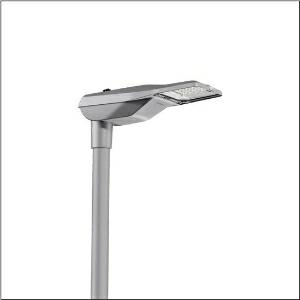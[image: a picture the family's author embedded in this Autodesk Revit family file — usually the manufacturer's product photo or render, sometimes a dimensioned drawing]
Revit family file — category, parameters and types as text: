
# Revit family: streetlight_sl_21_iq_micro___st1_0a_5xe1d31v08db_4967
name_source: partatom
category: Lighting Fixtures
units: mm (PartAtom-declared; Revit-internal decimal feet)

## family parameters
Cut with Voids When Loaded = No
Host = Face
Light Source = No
Part Type = Normal
Room Calculation Point = No
Round Connector Dimension = Use Diameter
Shared = No

## types (1)
- --- (1 x LED, 5110 lm, 39.1 W, 3000K)
    Apparent Load = 39 VA
    CIE Flux Codes = 37 72 97 100 100
    Color Rendering = 70
    Color Temperature = 3000K
    Default Elevation = 1800 mm
    Description = Streetlight SL 21 iQ micro, mast luminaire, primary light control with lens, of PMMA, primary optical cover: cover, of toughened safety glass, transparent, light distribution: ST1.0a, light emission: direct distribution, primary light characteristic: asymmetric, installation type: post-top, side-entry, LED, High Power LED, rated luminous flux: 5.110lm, luminous efficacy: 131lm/W, light colour: 730, colour temperature: 3000K, control gear: iQ-Street Remote, D4i with power reduction, control: pre-setting: logarithmic dimming characteristic, Street-Remote, Auto-Match, Temp-Guard, Lumen-Switch, Night-Set, Smart-Wire, Light-Fading, Desk-Remote (wireless, voltage-free reading and setting of iQ features in the workshop via application-optimized NFC function/RFID function), optimised constant luminous flux control (CLO 2.0), mains connection: 220..240V, AC, 50/60Hz, start of lifetime: 39W, end of service life: 41W, reduction: 17W, luminaire housing, of diecast aluminium, powder-coated, SITECO metallic grey (DB 702S), corrosivity category C5 high according to DIN EN ISO 12944, please order mast flange separately, inclination adjustable: 0°, 5°, 10°, 15°, sealing non-destructively replaceable, multi-level sealing system, length: 528mm, width: 235mm, height: 110mm, mast flange for spigot size: 42mm (side-entry): 5XC10008XM4, 60/48mm (side-entry/post-top): 5XC10108XM2, 76/60mm (side-entry/post-top): 5XC10108XM1, mounting height: 4..8m, Smart Interface above, protection rating (complete): IP66, insulation class (complete): insulation class II (safety insulation), certification: CE, ENEC, ENEC+, VDE, impact resistance: IK10, permissible operating ambient temperature for outdoor applications: -40..+50°C, standard-compliant lighting for roads and squares, packaging unit: 1 piece

Light Distribution: ST1.0a
    Height = 110 mm
    Lamp = 1 x LED
    Lamp Light Flux = 5110 lm
    Lamp Power = 39.1 W
    Lamp count = 1
    Length = 528 mm
    Luminous efficacy = 131 lm/W
    Manufacturer = Siteco
    ModVariant = No
    Model = 5XE1D31V08DB
    Number of Poles = 1
    OnlyDefault = Yes
    Power Factor = 1
    Product Name = Streetlight SL 21 iQ micro | ST1.0a
    Product group = mast luminaire | pylon top
    ProductGroupID = 6100
    Protection Class = Protection class II
    Protection Degree = IP 66
    RLX_Detail_Level = 1
    RLX_Emergency_Light_Flux = 0 lm
    RLX_Emergency_Type = 0
    RLX_Emergency_Type_DB = No
    RlxData = <blob elided: 98785 chars, md5=16df24e5>
    Socket = socket
    Standby Power = 0 W
    System Light Flux = 5110 lm
    System Power = 39 W
    Type Comments = factory setting: luminous flux: 100 % | dim-lin: 254 | 765 mA
    Type Image = l_1277292.jpg
    URL = http://relux.com
    VarID = @adj_115769
    Voltage = 0 V
    Weight = 0.00 kg
    Width = 235 mm

## geometry (parser evidence)
native form markers: Blend x4, Sweep x9
no freeform markers — native parametric forms only
